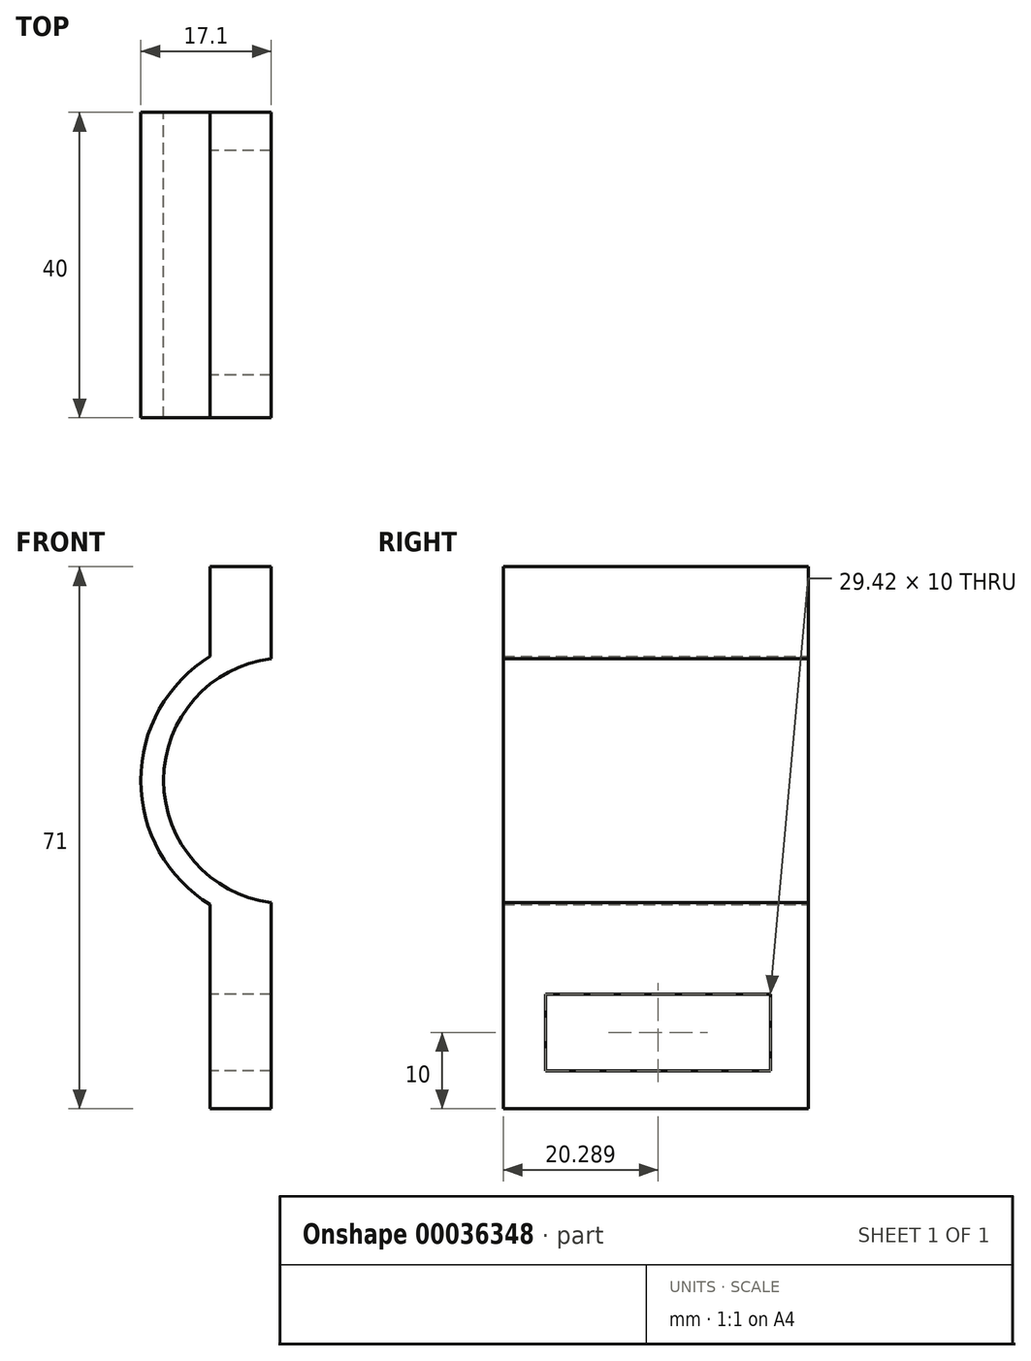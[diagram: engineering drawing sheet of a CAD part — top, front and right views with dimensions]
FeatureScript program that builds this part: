
annotation { "Feature Type Name" : "Feature", "Feature Type Description" : "" }
export const myFeature = defineFeature(function(context is Context, id is Id, definition is map)
    precondition{}
    {
        {
            var Q0;
            Q0=qCreatedBy(makeId("Front.planeOp"),FACE);
            var sketch = newSketch(context, id + "F0", { "sketchPlane" : qUnion([Q0])});
            skCircle(sketch, "E0", {"center": v(0, 0) * mm, "radius": 16.1 * mm, "construction": true});
            skLineSegment(sketch, "E1", {"start": v(0, 31.9) * mm, "end": v(0, -39.24) * mm, "construction": true});
            skLineSegment(sketch, "E2", {"start": v(-2, 15.98) * mm, "end": v(-2, 28) * mm});
            skLineSegment(sketch, "E3", {"start": v(-2, 28) * mm, "end": v(-10, 28) * mm});
            skLineSegment(sketch, "E4", {"start": v(-10, 28) * mm, "end": v(-10, 16.27) * mm});
            skLineSegment(sketch, "E5", {"start": v(-10, -16.27) * mm, "end": v(-10, -28) * mm});
            skLineSegment(sketch, "E6", {"start": v(-2, -28) * mm, "end": v(-2, -15.98) * mm});
            skArc(sketch, "E7", {"start": v(-2, 15.98) * mm, "mid": v(-16.1, 0) * mm, "end": v(-2, -15.98) * mm});
            skArc(sketch, "E8.0", {"start": v(-10, 16.27) * mm, "mid": v(-19.1, 0) * mm, "end": v(-10, -16.27) * mm});
            skLineSegment(sketch, "E9", {"start": v(-10, -28) * mm, "end": v(-2, -28) * mm, "construction": true});
            skLineSegment(sketch, "E10", {"start": v(-10, -28) * mm, "end": v(-10, -43) * mm});
            skLineSegment(sketch, "E11", {"start": v(-10, -43) * mm, "end": v(-2, -43) * mm});
            skLineSegment(sketch, "E12", {"start": v(-2, -43) * mm, "end": v(-2, -28) * mm});
            skSolve(sketch);
        }
        {
            var Q0;
            Q0 = qSketchRegion(id + "F0", true);
            extrude(context, id + "F1", {"entities" : qUnion([Q0]), "depth" : 40 * mm});
        }
        {
            var Q0;
            Q0=makeQuery(id+"F1.opExtrude","SWEPT_FACE",FACE,{"disambiguationData":[OSD([sQuery(id+"F0.wireOp",EDGE,"E5")])]});
            var sketch = newSketch(context, id + "F2", { "sketchPlane" : qUnion([Q0])});
            skLineSegment(sketch, "E13.bottom", {"start": v(5, -38) * mm, "end": v(34.42, -38) * mm});
            skLineSegment(sketch, "E13.top", {"start": v(5, -28) * mm, "end": v(34.42, -28) * mm});
            skLineSegment(sketch, "E13.left", {"start": v(5, -38) * mm, "end": v(5, -28) * mm});
            skLineSegment(sketch, "E13.right", {"start": v(34.42, -38) * mm, "end": v(34.42, -28) * mm});
            skSolve(sketch);
        }
        {
            var Q0;
            Q0 = qSketchRegion(id + "F2", true);
            extrude(context, id + "F3", {"entities" : qUnion([Q0]), "operationType" : NewBodyOperationType.REMOVE, "endBound" : BoundingType.THROUGH_ALL, "oppositeDirection" : true, "depth" : 25 * mm});
        }
    });
